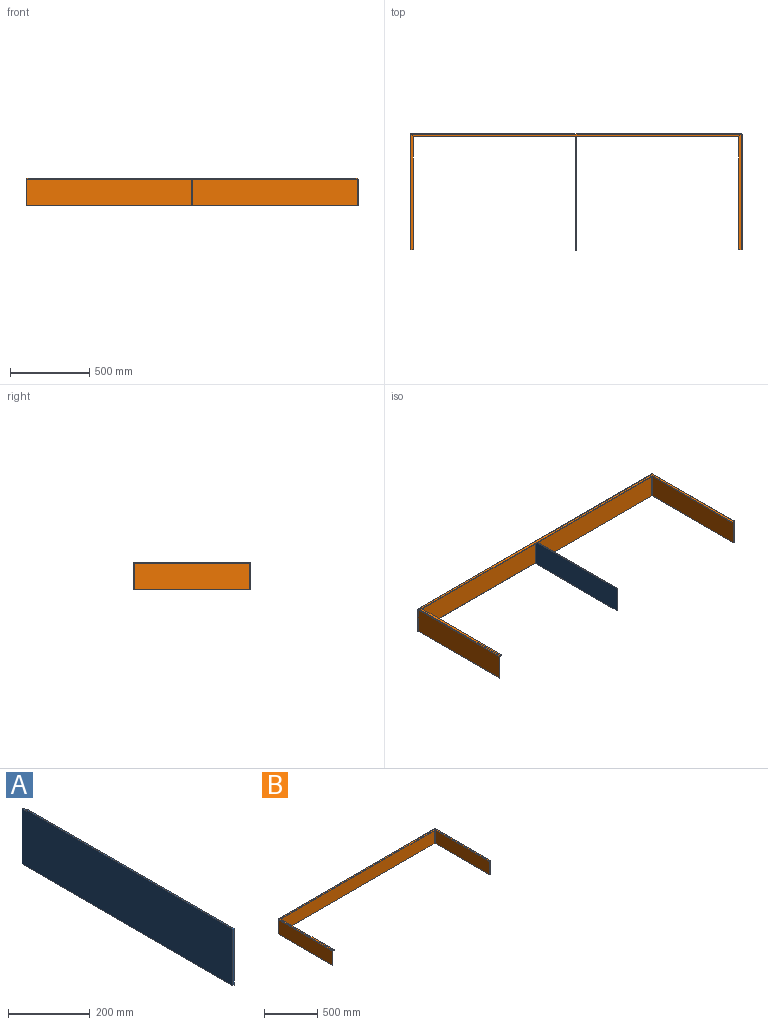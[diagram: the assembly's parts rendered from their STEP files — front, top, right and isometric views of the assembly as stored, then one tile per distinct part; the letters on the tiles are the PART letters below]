
ASSEMBLY  parts=2 mates=1
PART A: 8 faces, bbox 4x730x170 mm
  f0: plane 730x170mm, normal (1,0,0), area 124020mm2, adj f1,f3,f4,f5,f6,f7
  f1: plane 714x4mm, normal (0,0,1), area 2856mm2, adj f0,f2,f4,f7
  f2: plane 730x170mm, normal (-1,0,0), area 124020mm2, adj f1,f3,f4,f5,f6,f7
  f3: plane 730x4mm, normal (0,0,-1), area 2920mm2, adj f0,f2,f4,f5
  f4: plane 170x4mm, normal (0,-1,0), area 680mm2, adj f0,f1,f2,f3
  f5: plane 165x4mm, normal (0,1,0), area 660mm2, adj f0,f2,f3,f6
  f6: plane 16x4mm, normal (0,0,1), area 64mm2, adj f0,f2,f5,f7
  f7: plane 5x4mm, normal (0,1,0), area 20mm2, adj f0,f1,f2,f6
PART B: 50 faces, bbox 2090x730x170 mm
  f0: plane 4x0.01mm, normal (0,0,1), area 0.1mm2, adj f3,f4,f37,f47
  f1: plane 164x4mm, normal (0,-1,0), area 656mm2, adj f2,f3,f4,f46
  f2: plane 724x4mm, normal (0,0,-1), area 2896mm2, adj f1,f3,f4,f38
  f3: plane 724x164mm, normal (1,0,0), area 118736mm2, adj f0,f1,f2,f40,f49
  f4: plane 724x164mm, normal (-1,0,0), area 118736mm2, adj f0,f1,f2,f39,f48
  f5: plane 4x0.01mm, normal (0,0,1), area 0.1mm2, adj f8,f9,f34,f37
  f6: plane 4x0.01mm, normal (0,0,1), area 0.1mm2, adj f8,f9,f25,f33
  f7: plane 2078x4mm, normal (0,0,-1), area 8312mm2, adj f8,f9,f24,f38
  f8: plane 2078x164mm, normal (0,-1,0), area 340792mm2, adj f5,f6,f7,f27,f36,f40
  f9: plane 2078x164mm, normal (0,1,0), area 340792mm2, adj f5,f6,f7,f26,f35,f39
  f10: plane 4x0.01mm, normal (0,0,1), area 0.1mm2, adj f13,f14,f21,f25
  f11: plane 164x4mm, normal (0,-1,0), area 656mm2, adj f12,f13,f14,f20
  f12: plane 724x4mm, normal (0,0,-1), area 2896mm2, adj f11,f13,f14,f24
  f13: plane 724x164mm, normal (-1,0,0), area 118736mm2, adj f10,f11,f12,f23,f27
  f14: plane 724x164mm, normal (1,0,0), area 118736mm2, adj f10,f11,f12,f22,f26
  f15: plane 709.99x4mm, normal (-1,0,0), area 2839.9mm2, adj f16,f17,f18,f19
  f16: plane 14x14mm, normal (-0.71,0.71,0), area 79.2mm2, adj f15,f18,f19,f21
  f17: plane 14x4mm, normal (0,-1,0), area 56mm2, adj f15,f18,f19,f20
  f18: plane 723.99x14mm, normal (0,0,-1), area 10037.8mm2, adj f15,f16,f17,f23
  f19: plane 723.99x14mm, normal (0,0,1), area 10037.8mm2, adj f15,f16,f17,f22
  f20: plane 6x6mm, normal (0,-1,0), area 25.1mm2, adj f11,f17,f22,f23
  f21: plane 6x6mm, normal (0,1,0), area 25.1mm2, adj f10,f16,f22,f23
  f22: cylinder r=6mm len=723.99mm, axis (0,-1,0), area 6823.4mm2, adj f14,f19,f20,f21
  f23: cylinder r=2mm len=723.99mm, axis (0,-1,0), area 2274.5mm2, adj f13,f18,f20,f21
  f24: plane 6x6mm, normal (0,0,-1), area 25.1mm2, adj f7,f12,f26,f27
  f25: plane 6x6mm, normal (0,0,1), area 25.1mm2, adj f6,f10,f26,f27
  f26: cylinder r=6mm len=164mm, axis (0,0,-1), area 1545.7mm2, adj f9,f14,f24,f25
  f27: cylinder r=2mm len=164mm, axis (0,0,-1), area 515.2mm2, adj f8,f13,f24,f25
  f28: plane 2049.97x4mm, normal (0,-1,0), area 8199.9mm2, adj f29,f30,f31,f32
  f29: plane 14x14mm, normal (-0.71,-0.71,0), area 79.2mm2, adj f28,f31,f32,f34
  f30: plane 14x14mm, normal (0.71,-0.71,0), area 79.2mm2, adj f28,f31,f32,f33
  f31: plane 2077.97x14mm, normal (0,0,-1), area 28895.6mm2, adj f28,f29,f30,f36
  f32: plane 2077.97x14mm, normal (0,0,1), area 28895.6mm2, adj f28,f29,f30,f35
  f33: plane 6x6mm, normal (1,0,0), area 25.1mm2, adj f6,f30,f35,f36
  f34: plane 6x6mm, normal (-1,0,0), area 25.1mm2, adj f5,f29,f35,f36
  f35: cylinder r=6mm len=2077.97mm, axis (1,0,0), area 19584.4mm2, adj f9,f32,f33,f34
  f36: cylinder r=2mm len=2077.97mm, axis (1,0,0), area 6528.1mm2, adj f8,f31,f33,f34
  f37: plane 6x6mm, normal (0,0,1), area 25.1mm2, adj f0,f5,f39,f40
  f38: plane 6x6mm, normal (0,0,-1), area 25.1mm2, adj f2,f7,f39,f40
  f39: cylinder r=6mm len=164mm, axis (0,0,1), area 1545.7mm2, adj f4,f9,f37,f38
  f40: cylinder r=2mm len=164mm, axis (0,0,1), area 515.2mm2, adj f3,f8,f37,f38
  f41: plane 709.99x4mm, normal (1,0,0), area 2839.9mm2, adj f42,f43,f44,f45
  f42: plane 14x4mm, normal (0,-1,0), area 56mm2, adj f41,f44,f45,f46
  f43: plane 14x14mm, normal (0.71,0.71,0), area 79.2mm2, adj f41,f44,f45,f47
  f44: plane 723.99x14mm, normal (0,0,-1), area 10037.8mm2, adj f41,f42,f43,f49
  f45: plane 723.99x14mm, normal (0,0,1), area 10037.8mm2, adj f41,f42,f43,f48
  f46: plane 6x6mm, normal (0,-1,0), area 25.1mm2, adj f1,f42,f48,f49
  f47: plane 6x6mm, normal (0,1,0), area 25.1mm2, adj f0,f43,f48,f49
  f48: cylinder r=6mm len=723.99mm, axis (0,-1,0), area 6823.4mm2, adj f4,f45,f46,f47
  f49: cylinder r=2mm len=723.99mm, axis (0,-1,0), area 2274.5mm2, adj f3,f44,f46,f47
PLACE A t=(1045,-4,85)mm
PLACE B at identity
MATE fastened A.f5 <-> B.f8  axis (0,1,0) through (1045,-4,0)mm
